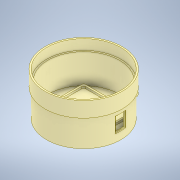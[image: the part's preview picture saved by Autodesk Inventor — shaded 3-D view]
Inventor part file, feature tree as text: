
AUTODESK INVENTOR PART (.ipt)
format: ipt  version: 2022 (Build 260153000, 153)  size: 223,744 bytes
history: native  units: mm
features: extrude x11, sketch x8, plane x3
ambient origin geometry x8: Origin, YZ Plane, XZ Plane, XY Plane, X Axis, Y Axis, Z Axis, Center Point
bodies: Solid1 (feature_tree)
feature tree (22):
  sketch  "Sketch1"  dims[d0=73.0mm d1=70.0mm]
  extrude  "Extrusion1"  Depth=70.0mm
  extrude  "Extrusion2"  Depth=3.0mm TaperAngle=0.0deg
  extrude  "Extrusion3"  Depth=46.2mm
  extrude  "Extrusion4"  Depth=2.0mm
  extrude  "Extrusion5"  Depth=19.5mm
  extrude  "Extrusion6"  Depth=7.5mm
  plane  "Work Plane2"
  sketch  "Sketch8"  dims[d14=2.0mm d15=0.0mm d16=19.5mm]
  extrude  "Extrusion9"  Depth=10.0mm
  extrude  "Extrusion10"  Depth=16.0mm
  plane  "Work Plane3"
  plane  "Work Plane5"
  extrude  "Extrusion14"  Depth=6.0mm TaperAngle=0.0deg
  extrude  "Extrusion16"  Depth=36.5mm
  extrude  "Extrusion17"  Depth=13.1mm
  sketch  "Sketch3"  dims[d2=3.0mm d3=0.0mm d4=120.0mm d5=0.0mm]
  sketch  "Sketch4"  dims[d9=2.0mm d10=0.0mm d11=46.2mm]
  sketch  "Sketch5"  dims[d12=46.2mm d13=2.0mm]
  sketch  "Sketch13"  dims[d17=7.5mm d18=18.0mm]
  sketch  "Sketch15"  dims[d19=0.0mm d20=0.0mm d21=10.0mm]
  sketch  "Sketch16"  dims[d22=36.5mm d23=16.0mm d24=6.0mm d25=0.0mm d37=36.5mm d38=13.1mm d39=8.5mm d40=0.0mm d41=15.0mm d42=10.5mm d43=15.0mm d44=3.0mm d45=0.0mm d46=1.0mm d47=0.0mm d48=-27.0mm d59=-88.0mm d61=40.0mm d62=3.0mm d63=0.0mm d66=0.0mm d67=0.0mm d68=76.0mm d69=73.0mm d70=10.0mm d71=5.0mm d72=0.0mm d73=0.0mm]
